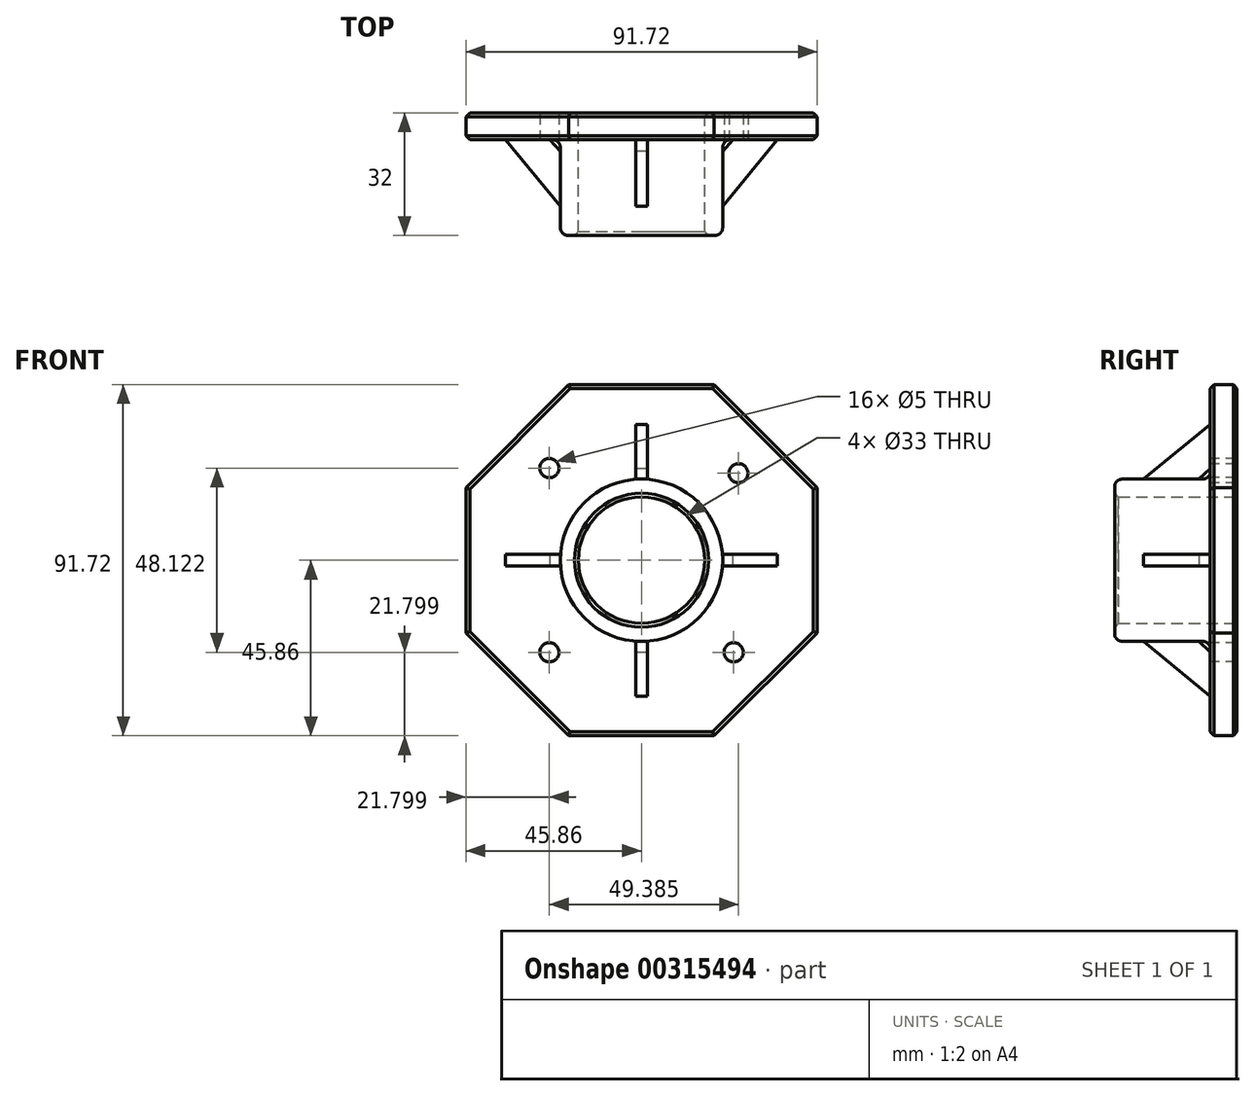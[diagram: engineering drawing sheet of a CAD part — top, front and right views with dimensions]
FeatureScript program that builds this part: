
annotation { "Feature Type Name" : "Feature", "Feature Type Description" : "" }
export const myFeature = defineFeature(function(context is Context, id is Id, definition is map)
    precondition{}
    {
        {
            var Q0;
            Q0=qCreatedBy(makeId("Front.planeOp"),FACE);
            var sketch = newSketch(context, id + "F0", { "sketchPlane" : qUnion([Q0])});
            skCircle(sketch, "E0.cCircle", {"center": v(0, 0) * mm, "radius": 45.86 * mm, "construction": true});
            skLineSegment(sketch, "E0.0", {"start": v(45.86, 19) * mm, "end": v(45.86, -19) * mm});
            skLineSegment(sketch, "E0.1", {"start": v(45.86, -19) * mm, "end": v(19, -45.86) * mm});
            skLineSegment(sketch, "E0.2", {"start": v(19, -45.86) * mm, "end": v(-19, -45.86) * mm});
            skLineSegment(sketch, "E0.3", {"start": v(-19, -45.86) * mm, "end": v(-45.86, -19) * mm});
            skLineSegment(sketch, "E0.4", {"start": v(-45.86, -19) * mm, "end": v(-45.86, 19) * mm});
            skLineSegment(sketch, "E0.5", {"start": v(-45.86, 19) * mm, "end": v(-19, 45.86) * mm});
            skLineSegment(sketch, "E0.6", {"start": v(-19, 45.86) * mm, "end": v(19, 45.86) * mm});
            skLineSegment(sketch, "E0.7", {"start": v(19, 45.86) * mm, "end": v(45.86, 19) * mm});
            skPoint(sketch, "E0.0.midPoint", {"position": v(45.86, 0) * mm});
            skCircle(sketch, "E1", {"center": v(0, 0) * mm, "radius": 16.5 * mm});
            skCircle(sketch, "E2", {"center": v(0, 0) * mm, "radius": 34.03 * mm, "construction": true});
            skLineSegment(sketch, "E3", {"start": v(-32.43, 32.43) * mm, "end": v(0, 0) * mm, "construction": true});
            skLineSegment(sketch, "E4", {"start": v(0, 0) * mm, "end": v(32.43, -32.43) * mm, "construction": true});
            skLineSegment(sketch, "E5", {"start": v(0, 0) * mm, "end": v(34.18, 30.68) * mm, "construction": true});
            skLineSegment(sketch, "E6", {"start": v(-32.43, -32.43) * mm, "end": v(0, 0) * mm, "construction": true});
            skPoint(sketch, "E7", {"position": v(25.32, 22.73) * mm});
            skPoint(sketch, "E8", {"position": v(-24.06, 24.06) * mm});
            skPoint(sketch, "E9", {"position": v(-24.06, -24.06) * mm});
            skPoint(sketch, "E10", {"position": v(24.06, -24.06) * mm});
            skSolve(sketch);
        }
        {
            var Q0;
            Q0 = qSketchRegion(id + "F0", true);
            extrude(context, id + "F1", {"entities" : qUnion([Q0]), "depth" : 7 * mm});
        }
        {
            var Q0;
            Q0=makeQuery(id+"F1.opExtrude","CAP_FACE",FACE,{"disambiguationData":[OSD([sQuery(id+"F0.wireOp",EDGE,"E0.0"),sQuery(id+"F0.wireOp",EDGE,"E0.1"),sQuery(id+"F0.wireOp",EDGE,"E0.2"),sQuery(id+"F0.wireOp",EDGE,"E0.3"),sQuery(id+"F0.wireOp",EDGE,"E0.4"),sQuery(id+"F0.wireOp",EDGE,"E0.5"),sQuery(id+"F0.wireOp",EDGE,"E0.6"),sQuery(id+"F0.wireOp",EDGE,"E0.7")])],"isStart":false});
            var sketch = newSketch(context, id + "F2", { "sketchPlane" : qUnion([Q0])});
            skCircle(sketch, "E11", {"center": v(0, 0) * mm, "radius": 21.19 * mm});
            skCircle(sketch, "E12", {"center": v(0, 0) * mm, "radius": 16.5 * mm});
            skSolve(sketch);
        }
        {
            var Q0;
            Q0 = qSketchRegion(id + "F2", true);
            extrude(context, id + "F3", {"entities" : qUnion([Q0]), "operationType" : NewBodyOperationType.ADD, "depth" : 25 * mm, "hasSecondDirection" : true, "secondDirectionOppositeDirection" : true, "secondDirectionDepth" : 7 * mm});
        }
        {
            var Q0;
            Q0=makeQuery(id+"F3.boolean.opBoolean","INTERSECT",EDGE,{"derivedFrom":[makeQuery(id+"F1.opExtrude","CAP_FACE",FACE,{"disambiguationData":[OSD([sQuery(id+"F0.wireOp",EDGE,"E0.0"),sQuery(id+"F0.wireOp",EDGE,"E0.1"),sQuery(id+"F0.wireOp",EDGE,"E0.2"),sQuery(id+"F0.wireOp",EDGE,"E0.3"),sQuery(id+"F0.wireOp",EDGE,"E0.4"),sQuery(id+"F0.wireOp",EDGE,"E0.5"),sQuery(id+"F0.wireOp",EDGE,"E0.6"),sQuery(id+"F0.wireOp",EDGE,"E0.7"),sQuery(id+"F0.wireOp",EDGE,"E1")])],"isStart":false}),makeQuery(id+"F3.opExtrude","SWEPT_FACE",FACE,{"disambiguationData":[OSD([sQuery(id+"F2.wireOp",EDGE,"E11")])]})]});
            fillet(context, id + "F4", {"entities" : qUnion([Q0]), "radius" : 2 * mm, "tangentPropagation" : true, "allowEdgeOverflow" : false});
        }
        {
            var Q0;
            Q0=makeQuery(id+"F3.opExtrude","CAP_EDGE",EDGE,{"disambiguationData":[OSD([sQuery(id+"F2.wireOp",EDGE,"E12")])],"isStart":false});
            var Q1;
            Q1=makeQuery(id+"F1.opExtrude","CAP_FACE",FACE,{"disambiguationData":[OSD([sQuery(id+"F0.wireOp",EDGE,"E0.0"),sQuery(id+"F0.wireOp",EDGE,"E0.1"),sQuery(id+"F0.wireOp",EDGE,"E0.2"),sQuery(id+"F0.wireOp",EDGE,"E0.3"),sQuery(id+"F0.wireOp",EDGE,"E0.4"),sQuery(id+"F0.wireOp",EDGE,"E0.5"),sQuery(id+"F0.wireOp",EDGE,"E0.6"),sQuery(id+"F0.wireOp",EDGE,"E0.7"),sQuery(id+"F0.wireOp",EDGE,"E1")])],"isStart":false});
            var Q2;
            Q2=makeQuery(id+"F1.opExtrude","CAP_FACE",FACE,{"disambiguationData":[OSD([sQuery(id+"F0.wireOp",EDGE,"E0.0"),sQuery(id+"F0.wireOp",EDGE,"E0.1"),sQuery(id+"F0.wireOp",EDGE,"E0.2"),sQuery(id+"F0.wireOp",EDGE,"E0.3"),sQuery(id+"F0.wireOp",EDGE,"E0.4"),sQuery(id+"F0.wireOp",EDGE,"E0.5"),sQuery(id+"F0.wireOp",EDGE,"E0.6"),sQuery(id+"F0.wireOp",EDGE,"E0.7"),sQuery(id+"F0.wireOp",EDGE,"E1")])],"isStart":true});
            chamfer(context, id + "F5", {"entities" : qUnion([Q0, Q1, Q2]), "width" : 1 * mm, "tangentPropagation" : true});
        }
        {
            var Q0;
            Q0=makeQuery(id+"F3.opExtrude","CAP_EDGE",EDGE,{"disambiguationData":[OSD([sQuery(id+"F2.wireOp",EDGE,"E11")])],"isStart":false});
            fillet(context, id + "F6", {"entities" : qUnion([Q0]), "radius" : 2 * mm, "tangentPropagation" : true, "allowEdgeOverflow" : false});
        }
        {
            var Q0;
            Q0=qCreatedBy(makeId("Top.planeOp"),FACE);
            var sketch = newSketch(context, id + "F7", { "sketchPlane" : qUnion([Q0])});
            skLineSegment(sketch, "E13", {"start": v(0, -33.6) * mm, "end": v(0, 8.73) * mm});
            skLineSegment(sketch, "E14", {"start": v(-21.19, -24.4) * mm, "end": v(-21.19, -9.97) * mm});
            skLineSegment(sketch, "E15", {"start": v(-35.51, -7) * mm, "end": v(-23.93, -7) * mm});
            skLineSegment(sketch, "E16", {"start": v(-21.17, -24.42) * mm, "end": v(-35.51, -7) * mm});
            skLineSegment(sketch, "E17", {"start": v(-21.19, -9.97) * mm, "end": v(-23.93, -7) * mm});
            skSolve(sketch);
        }
        {
            var Q0;
            {var subQ0=sQuery(id+"F7.wireOp",EDGE,"E14");Q0=makeQuery(id+"F7.imprint","IMPRINT",FACE,{"disambiguationData":[TD([[makeQuery(id+"F7.imprint","IMPRINT",EDGE,{"derivedFrom":subQ0}),1.0]])]});}
            extrude(context, id + "F8", {"entities" : qUnion([Q0]), "operationType" : NewBodyOperationType.ADD, "depth" : 1.5 * mm, "hasSecondDirection" : true, "secondDirectionOppositeDirection" : true, "secondDirectionDepth" : 1.5 * mm});
        }
        {
            var Q0;
            Q0=makeQuery(id+"F1.opExtrude","SWEPT_BODY",BODY,{"disambiguationData":[OSD([sQuery(id+"F0.wireOp",EDGE,"E0.0"),sQuery(id+"F0.wireOp",EDGE,"E0.1"),sQuery(id+"F0.wireOp",EDGE,"E0.2"),sQuery(id+"F0.wireOp",EDGE,"E0.3"),sQuery(id+"F0.wireOp",EDGE,"E0.4"),sQuery(id+"F0.wireOp",EDGE,"E0.5"),sQuery(id+"F0.wireOp",EDGE,"E0.6"),sQuery(id+"F0.wireOp",EDGE,"E0.7"),sQuery(id+"F0.wireOp",EDGE,"E1")])]});
            var Q1;
            {var subQ0=sQuery(id+"F2.wireOp",EDGE,"E12");Q1=makeQuery(id+"F5.opChamfer","BLEND_EDGE",EDGE,{"blendedFrom":[makeQuery(id+"F3.opExtrude","CAP_EDGE",EDGE,{"disambiguationData":[OSD([subQ0])],"isStart":false}),makeQuery(id+"F3.boolean.opBoolean","MERGE",FACE,{"derivedFrom":[makeQuery(id+"F1.opExtrude","SWEPT_FACE",FACE,{"disambiguationData":[OSD([sQuery(id+"F0.wireOp",EDGE,"E1")])]}),makeQuery(id+"F3.opExtrude","SWEPT_FACE",FACE,{"disambiguationData":[OSD([subQ0])]})]})],"blendedInto":[makeQuery(id+"F3.boolean.opBoolean","MERGE",FACE,{"derivedFrom":[makeQuery(id+"F1.opExtrude","SWEPT_FACE",FACE,{"disambiguationData":[OSD([sQuery(id+"F0.wireOp",EDGE,"E1")])]}),makeQuery(id+"F3.opExtrude","SWEPT_FACE",FACE,{"disambiguationData":[OSD([subQ0])]})]})]});}
            circularPattern(context, id + "F9", {"entities" : qUnion([Q0]), "axis" : qUnion([Q1]), "angle" : 360 * degree, "instanceCount" : 4, "equalSpace" : true});
        }
        {
            var Q0;
            Q0=sQuery(id+"F0.wireOp",VERTEX,"E7");
            var Q1;
            Q1=sQuery(id+"F0.wireOp",VERTEX,"E8");
            var Q2;
            Q2=sQuery(id+"F0.wireOp",VERTEX,"E9");
            var Q3;
            Q3=sQuery(id+"F0.wireOp",VERTEX,"E10");
            var Q4;
            Q4=makeQuery(id+"F1.opExtrude","SWEPT_BODY",BODY,{"disambiguationData":[OSD([sQuery(id+"F0.wireOp",EDGE,"E0.0"),sQuery(id+"F0.wireOp",EDGE,"E0.1"),sQuery(id+"F0.wireOp",EDGE,"E0.2"),sQuery(id+"F0.wireOp",EDGE,"E0.3"),sQuery(id+"F0.wireOp",EDGE,"E0.4"),sQuery(id+"F0.wireOp",EDGE,"E0.5"),sQuery(id+"F0.wireOp",EDGE,"E0.6"),sQuery(id+"F0.wireOp",EDGE,"E0.7"),sQuery(id+"F0.wireOp",EDGE,"E1")])]});
            var Q5;
            Q5=makeQuery(id+"F9.opPattern","COPY",BODY,{"derivedFrom":makeQuery(id+"F1.opExtrude","SWEPT_BODY",BODY,{"disambiguationData":[OSD([sQuery(id+"F0.wireOp",EDGE,"E0.0"),sQuery(id+"F0.wireOp",EDGE,"E0.1"),sQuery(id+"F0.wireOp",EDGE,"E0.2"),sQuery(id+"F0.wireOp",EDGE,"E0.3"),sQuery(id+"F0.wireOp",EDGE,"E0.4"),sQuery(id+"F0.wireOp",EDGE,"E0.5"),sQuery(id+"F0.wireOp",EDGE,"E0.6"),sQuery(id+"F0.wireOp",EDGE,"E0.7"),sQuery(id+"F0.wireOp",EDGE,"E1")])]}),"instanceName":"1"});
            var Q6;
            Q6=makeQuery(id+"F9.opPattern","COPY",BODY,{"derivedFrom":makeQuery(id+"F1.opExtrude","SWEPT_BODY",BODY,{"disambiguationData":[OSD([sQuery(id+"F0.wireOp",EDGE,"E0.0"),sQuery(id+"F0.wireOp",EDGE,"E0.1"),sQuery(id+"F0.wireOp",EDGE,"E0.2"),sQuery(id+"F0.wireOp",EDGE,"E0.3"),sQuery(id+"F0.wireOp",EDGE,"E0.4"),sQuery(id+"F0.wireOp",EDGE,"E0.5"),sQuery(id+"F0.wireOp",EDGE,"E0.6"),sQuery(id+"F0.wireOp",EDGE,"E0.7"),sQuery(id+"F0.wireOp",EDGE,"E1")])]}),"instanceName":"2"});
            var Q7;
            Q7=makeQuery(id+"F9.opPattern","COPY",BODY,{"derivedFrom":makeQuery(id+"F1.opExtrude","SWEPT_BODY",BODY,{"disambiguationData":[OSD([sQuery(id+"F0.wireOp",EDGE,"E0.0"),sQuery(id+"F0.wireOp",EDGE,"E0.1"),sQuery(id+"F0.wireOp",EDGE,"E0.2"),sQuery(id+"F0.wireOp",EDGE,"E0.3"),sQuery(id+"F0.wireOp",EDGE,"E0.4"),sQuery(id+"F0.wireOp",EDGE,"E0.5"),sQuery(id+"F0.wireOp",EDGE,"E0.6"),sQuery(id+"F0.wireOp",EDGE,"E0.7"),sQuery(id+"F0.wireOp",EDGE,"E1")])]}),"instanceName":"3"});
            hole(context, id + "F10", {"style" : HoleStyle.SIMPLE, "endStyle" : HoleEndStyle.THROUGH, "oppositeDirection" : true, "standardTappedOrClearance" : lookupTablePath({ "standard" : "ISO", "fit" : "Normal", "size" : "M5", "type" : "Abstand" }), "standardBlindInLast" : lookupTablePath({ "fit" : "Standard", "standard" : "ISO", "size" : "M5", "type" : "Abstand" }), "holeDiameter" : 5 * mm, "isTappedThrough" : true, "tappedDepth" : 12 * mm, "tapClearance" : 3, "locations" : qUnion([Q0, Q1, Q2, Q3]), "scope" : qUnion([Q4, Q5, Q6, Q7])});
        }
    });
